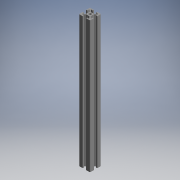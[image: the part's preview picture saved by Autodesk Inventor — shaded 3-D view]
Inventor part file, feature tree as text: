
AUTODESK INVENTOR PART (.ipt)
format: ipt  version: 2017.3 (Build 213256000, 256)  size: 207,360 bytes
history: native  units: mm (DEFAULTED — no unit token found)
features: other x7, sketch x2, extrude x1, hole x1
ambient origin geometry x8: Origin, YZ Plane, XZ Plane, XY Plane, X Axis, Y Axis, Z Axis, Center Point
bodies: Solid1 (feature_tree)
feature tree (11):
  extrude  "Extrusion1"  TaperAngle=0.0deg  [1 undecoded]
  hole  "Hole1"  [1 undecoded]
  other  "C1_XY"
  other  "C1_YZ"
  other  "C1_ZX"
  other  "C1_X"
  other  "C1_Y"
  other  "C1_Z"
  other  "C1_Center"
  sketch  "Sketch_75"  dims[d2=4.2mm d3=6.0mm d4=4.0mm d5=2.0mm d6=90.0deg d7=237.0mm d8=0.0mm d9=0.0mm]
  sketch  "Sketch2"  dims[d0=237.0mm d1=0.0mm]
note: 2 required parameter values undecoded (feature->parameter linkage not recoverable at this tier; creation-order binding heuristic only, values carry confidence <= 0.55)
